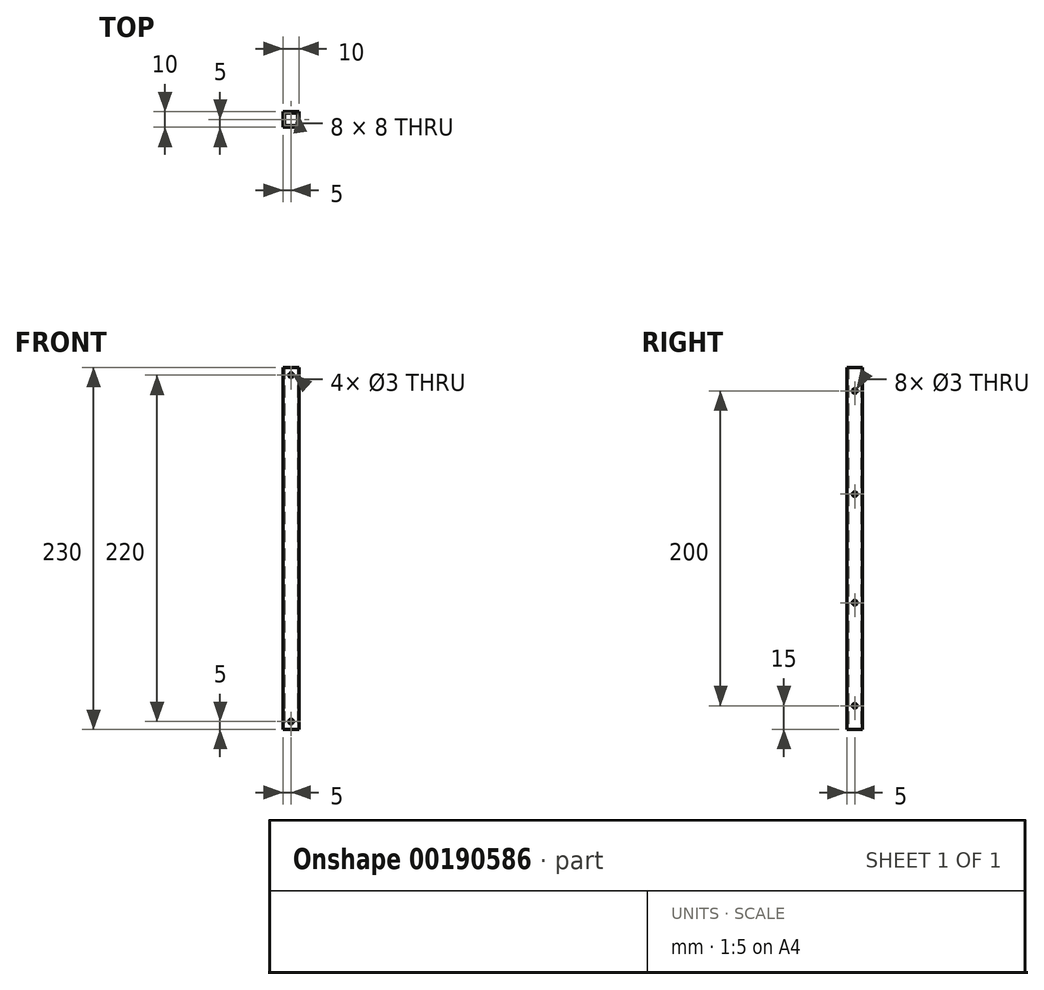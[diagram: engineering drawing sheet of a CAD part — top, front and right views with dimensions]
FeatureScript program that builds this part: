
annotation { "Feature Type Name" : "Feature", "Feature Type Description" : "" }
export const myFeature = defineFeature(function(context is Context, id is Id, definition is map)
    precondition{}
    {
        {
            var Q0;
            Q0=qCreatedBy(makeId("Top.planeOp"),FACE);
            var sketch = newSketch(context, id + "F0", { "sketchPlane" : qUnion([Q0])});
            skLineSegment(sketch, "E0.bottom", {"start": v(-5, -5) * mm, "end": v(5, -5) * mm});
            skLineSegment(sketch, "E0.top", {"start": v(-5, 5) * mm, "end": v(5, 5) * mm});
            skLineSegment(sketch, "E0.left", {"start": v(-5, -5) * mm, "end": v(-5, 5) * mm});
            skLineSegment(sketch, "E0.right", {"start": v(5, -5) * mm, "end": v(5, 5) * mm});
            skPoint(sketch, "E0.middle", {"position": v(0, 0) * mm});
            skLineSegment(sketch, "E1.bottom", {"start": v(-4, -4) * mm, "end": v(4, -4) * mm});
            skLineSegment(sketch, "E1.top", {"start": v(-4, 4) * mm, "end": v(4, 4) * mm});
            skLineSegment(sketch, "E1.left", {"start": v(-4, -4) * mm, "end": v(-4, 4) * mm});
            skLineSegment(sketch, "E1.right", {"start": v(4, -4) * mm, "end": v(4, 4) * mm});
            skSolve(sketch);
        }
        {
            var Q0;
            Q0 = qSketchRegion(id + "F0", true);
            extrude(context, id + "F1", {"entities" : qUnion([Q0]), "depth" : 230 * mm});
        }
        {
            var Q0;
            Q0=makeQuery(id+"F1.opExtrude","SWEPT_FACE",FACE,{"disambiguationData":[OSD([sQuery(id+"F0.wireOp",EDGE,"E0.right")])]});
            var sketch = newSketch(context, id + "F2", { "sketchPlane" : qUnion([Q0])});
            skLineSegment(sketch, "E2", {"start": v(0, 230) * mm, "end": v(0, 0) * mm, "construction": true});
            skLineSegment(sketch, "E3", {"start": v(-5, 115) * mm, "end": v(5, 115) * mm, "construction": true});
            skCircle(sketch, "E4", {"center": v(0, 80.5) * mm, "radius": 1.5 * mm});
            skCircle(sketch, "E5", {"center": v(0, 15) * mm, "radius": 1.5 * mm});
            skCircle(sketch, "E6.MirrorC", {"center": v(0, 149.5) * mm, "radius": 1.5 * mm});
            skCircle(sketch, "E7.MirrorC", {"center": v(0, 215) * mm, "radius": 1.5 * mm});
            skSolve(sketch);
        }
        {
            var Q0;
            Q0 = qSketchRegion(id + "F2", true);
            extrude(context, id + "F3", {"entities" : qUnion([Q0]), "operationType" : NewBodyOperationType.REMOVE, "oppositeDirection" : true, "depth" : 25 * mm});
        }
        {
            var Q0;
            Q0=makeQuery(id+"F1.opExtrude","SWEPT_FACE",FACE,{"disambiguationData":[OSD([sQuery(id+"F0.wireOp",EDGE,"E0.bottom")])]});
            var sketch = newSketch(context, id + "F4", { "sketchPlane" : qUnion([Q0])});
            skLineSegment(sketch, "E8", {"start": v(0, 230) * mm, "end": v(0, 0) * mm, "construction": true});
            skLineSegment(sketch, "E9", {"start": v(-5, 115) * mm, "end": v(5, 115) * mm, "construction": true});
            skCircle(sketch, "E10", {"center": v(0, 5) * mm, "radius": 1.5 * mm});
            skCircle(sketch, "E11.MirrorC", {"center": v(0, 225) * mm, "radius": 1.5 * mm});
            skSolve(sketch);
        }
        {
            var Q0;
            Q0 = qSketchRegion(id + "F4", true);
            extrude(context, id + "F5", {"entities" : qUnion([Q0]), "operationType" : NewBodyOperationType.REMOVE, "oppositeDirection" : true, "depth" : 25 * mm});
        }
    });
